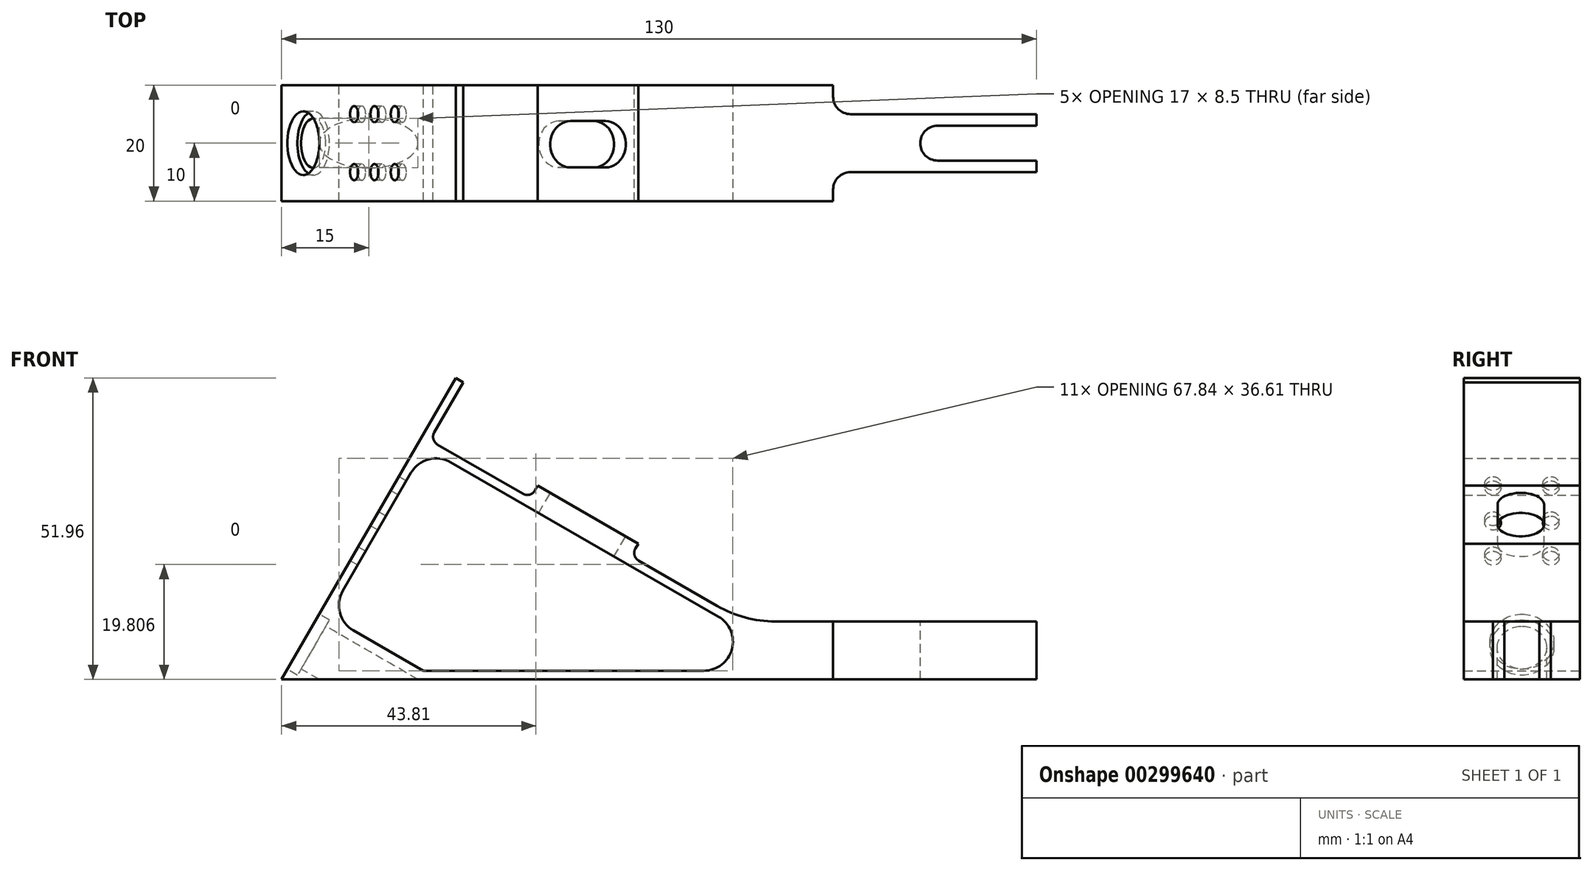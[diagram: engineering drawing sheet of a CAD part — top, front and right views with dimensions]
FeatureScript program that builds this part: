
annotation { "Feature Type Name" : "Feature", "Feature Type Description" : "" }
export const myFeature = defineFeature(function(context is Context, id is Id, definition is map)
    precondition{}
    {
        {
            var Q0;
            Q0=qCreatedBy(makeId("Front.planeOp"),FACE);
            var sketch = newSketch(context, id + "F0", { "sketchPlane" : qUnion([Q0])});
            skLineSegment(sketch, "E0", {"start": v(-65, 0) * mm, "end": v(-35, 51.96) * mm});
            skLineSegment(sketch, "E1", {"start": v(-35, 51.96) * mm, "end": v(-33.7, 51.21) * mm});
            skLineSegment(sketch, "E2", {"start": v(-33.7, 51.21) * mm, "end": v(-38.7, 42.55) * mm});
            skLineSegment(sketch, "E3", {"start": v(-38.15, 40.5) * mm, "end": v(-23.43, 32) * mm});
            skLineSegment(sketch, "E4", {"start": v(-21.38, 32.55) * mm, "end": v(-20.88, 33.42) * mm});
            skLineSegment(sketch, "E5", {"start": v(-20.88, 33.42) * mm, "end": v(-3.56, 23.42) * mm});
            skLineSegment(sketch, "E6", {"start": v(-3.56, 23.42) * mm, "end": v(-4.06, 22.55) * mm});
            skLineSegment(sketch, "E7", {"start": v(-3.51, 20.5) * mm, "end": v(10.04, 12.68) * mm});
            skLineSegment(sketch, "E8", {"start": v(20.04, 10) * mm, "end": v(65, 10) * mm});
            skLineSegment(sketch, "E9", {"start": v(65, 10) * mm, "end": v(65, 0) * mm});
            skLineSegment(sketch, "E10", {"start": v(-65, 0) * mm, "end": v(65, 0) * mm});
            skLineSegment(sketch, "E11", {"start": v(-22.13, 31.25) * mm, "end": v(-55.19, 50.34) * mm, "construction": true});
            skPoint(sketch, "E12.visualSharp", {"position": v(14.68, 10) * mm});
            skArc(sketch, "E12.filletArc", {"start": v(10.04, 12.68) * mm, "mid": v(14.86, 10.68) * mm, "end": v(20.04, 10) * mm});
            skPoint(sketch, "E13.visualSharp", {"position": v(-4.8, 21.25) * mm});
            skArc(sketch, "E13.filletArc", {"start": v(-4.06, 22.55) * mm, "mid": v(-4.2, 21.41) * mm, "end": v(-3.51, 20.5) * mm});
            skPoint(sketch, "E14.visualSharp", {"position": v(-22.13, 31.25) * mm});
            skArc(sketch, "E14.filletArc", {"start": v(-23.43, 32) * mm, "mid": v(-22.3, 31.85) * mm, "end": v(-21.38, 32.55) * mm});
            skPoint(sketch, "E15.visualSharp", {"position": v(-39.45, 41.25) * mm});
            skArc(sketch, "E15.filletArc", {"start": v(-38.7, 42.55) * mm, "mid": v(-38.85, 41.41) * mm, "end": v(-38.15, 40.5) * mm});
            skLineSegment(sketch, "E16", {"start": v(-54.45, 15.27) * mm, "end": v(-42.7, 35.62) * mm});
            skLineSegment(sketch, "E17", {"start": v(-35.87, 37.45) * mm, "end": v(10.24, 10.83) * mm});
            skLineSegment(sketch, "E18", {"start": v(7.74, 1.5) * mm, "end": v(-40.6, 1.5) * mm});
            skLineSegment(sketch, "E19", {"start": v(-40.6, 1.5) * mm, "end": v(-52.62, 8.44) * mm});
            skPoint(sketch, "E20.visualSharp", {"position": v(26.4, 1.5) * mm});
            skArc(sketch, "E20.filletArc", {"start": v(7.74, 1.5) * mm, "mid": v(12.57, 5.2) * mm, "end": v(10.24, 10.83) * mm});
            skPoint(sketch, "E21.visualSharp", {"position": v(-56.95, 10.94) * mm});
            skArc(sketch, "E21.filletArc", {"start": v(-54.45, 15.27) * mm, "mid": v(-54.95, 11.48) * mm, "end": v(-52.62, 8.44) * mm});
            skPoint(sketch, "E22.visualSharp", {"position": v(-40.2, 39.95) * mm});
            skArc(sketch, "E22.filletArc", {"start": v(-35.87, 37.45) * mm, "mid": v(-39.66, 37.95) * mm, "end": v(-42.7, 35.62) * mm});
            skSolve(sketch);
        }
        {
            var Q0;
            Q0=makeQuery(id+"F0.imprint","IMPRINT",FACE,{"disambiguationData":[TD([[makeQuery(id+"F0.imprint","IMPRINT",EDGE,{"derivedFrom":sQuery(id+"F0.wireOp",EDGE,"E0")}),-1.0]])]});
            extrude(context, id + "F1", {"entities" : qUnion([Q0]), "depth" : 20 * mm});
        }
        {
            var Q0;
            Q0=makeQuery(id+"F1.opExtrude","SWEPT_FACE",FACE,{"disambiguationData":[OSD([sQuery(id+"F0.wireOp",EDGE,"E8")])]});
            var sketch = newSketch(context, id + "F2", { "sketchPlane" : qUnion([Q0])});
            skArc(sketch, "E23", {"start": v(48, -7) * mm, "mid": v(45, -10) * mm, "end": v(48, -13) * mm});
            skLineSegment(sketch, "E24", {"start": v(48, -7) * mm, "end": v(65, -7) * mm});
            skLineSegment(sketch, "E25", {"start": v(48, -13) * mm, "end": v(65, -13) * mm});
            skLineSegment(sketch, "E26", {"start": v(65, -13) * mm, "end": v(65, -7) * mm});
            skLineSegment(sketch, "E27", {"start": v(65, -2.04) * mm, "end": v(65, -17.96) * mm});
            skLineSegment(sketch, "E28", {"start": v(65, -5) * mm, "end": v(33, -5) * mm});
            skLineSegment(sketch, "E29", {"start": v(30, -2) * mm, "end": v(30, 0) * mm});
            skLineSegment(sketch, "E30", {"start": v(30, -18) * mm, "end": v(30, -20) * mm});
            skLineSegment(sketch, "E31", {"start": v(33, -15) * mm, "end": v(65, -15) * mm});
            skPoint(sketch, "E32.visualSharp", {"position": v(30, -15) * mm});
            skArc(sketch, "E32.filletArc", {"start": v(33, -15) * mm, "mid": v(30.88, -15.88) * mm, "end": v(30, -18) * mm});
            skPoint(sketch, "E33.visualSharp", {"position": v(30, -5) * mm});
            skArc(sketch, "E33.filletArc", {"start": v(30, -2) * mm, "mid": v(30.88, -4.12) * mm, "end": v(33, -5) * mm});
            skLineSegment(sketch, "E34", {"start": v(30, 0) * mm, "end": v(65, 0) * mm});
            skLineSegment(sketch, "E35", {"start": v(65, 0) * mm, "end": v(65, -5) * mm});
            skLineSegment(sketch, "E36", {"start": v(65, -15) * mm, "end": v(65, -20) * mm});
            skLineSegment(sketch, "E37", {"start": v(65, -20) * mm, "end": v(30, -20) * mm});
            skSolve(sketch);
        }
        {
            var Q0;
            Q0=makeQuery(id+"F2.imprint","IMPRINT",FACE,{"disambiguationData":[TD([[makeQuery(id+"F2.imprint","IMPRINT",EDGE,{"derivedFrom":sQuery(id+"F2.wireOp",EDGE,"E30")}),1.0]])]});
            var Q1;
            Q1=makeQuery(id+"F2.imprint","IMPRINT",FACE,{"disambiguationData":[TD([[makeQuery(id+"F2.imprint","IMPRINT",EDGE,{"derivedFrom":sQuery(id+"F2.wireOp",EDGE,"E23")}),1.0]])]});
            var Q2;
            {var subQ1=sQuery(id+"F2.wireOp",EDGE,"E28");Q2=makeQuery(id+"F2.imprint","IMPRINT",FACE,{"disambiguationData":[TD([[makeQuery(id+"F2.imprint","IMPRINT",EDGE,{"derivedFrom":subQ1}),-1.0]])]});}
            extrude(context, id + "F3", {"entities" : qUnion([Q0, Q1, Q2]), "operationType" : NewBodyOperationType.REMOVE, "oppositeDirection" : true, "depth" : 25 * mm});
        }
        {
            var Q0;
            Q0=makeQuery(id+"F1.opExtrude","SWEPT_FACE",FACE,{"disambiguationData":[OSD([sQuery(id+"F0.wireOp",EDGE,"E5")])]});
            cPlane(context, id + "F4", {"entities" : qUnion([Q0]), "cplaneType" : CPlaneType.OFFSET, "offset" : 0 * mm, "width" : 150 * mm, "height" : 150 * mm});
        }
        {
            var Q0;
            Q0=qCreatedBy(id+"F4.planeOp",FACE);
            var sketch = newSketch(context, id + "F5", { "sketchPlane" : qUnion([Q0])});
            skArc(sketch, "E38", {"start": v(-28.3, -6.2) * mm, "mid": v(-32.3, -10.2) * mm, "end": v(-28.3, -14.2) * mm});
            skArc(sketch, "E39", {"start": v(-21.3, -14.2) * mm, "mid": v(-17.3, -10.2) * mm, "end": v(-21.3, -6.2) * mm});
            skLineSegment(sketch, "E40", {"start": v(-28.3, -6.2) * mm, "end": v(-21.3, -6.2) * mm});
            skLineSegment(sketch, "E41", {"start": v(-28.3, -14.2) * mm, "end": v(-21.3, -14.2) * mm});
            skSolve(sketch);
        }
        {
            var Q0;
            Q0 = qSketchRegion(id + "F5", true);
            extrude(context, id + "F6", {"entities" : qUnion([Q0]), "operationType" : NewBodyOperationType.REMOVE, "endBound" : BoundingType.UP_TO_NEXT, "oppositeDirection" : true, "depth" : 25 * mm});
        }
        {
            var Q0;
            Q0=makeQuery(id+"F1.opExtrude","SWEPT_FACE",FACE,{"disambiguationData":[OSD([sQuery(id+"F0.wireOp",EDGE,"E0")])]});
            cPlane(context, id + "F7", {"entities" : qUnion([Q0]), "cplaneType" : CPlaneType.OFFSET, "offset" : 0 * mm, "width" : 150 * mm, "height" : 150 * mm});
        }
        {
            var Q0;
            Q0=qCreatedBy(id+"F7.planeOp",FACE);
            var sketch = newSketch(context, id + "F8", { "sketchPlane" : qUnion([Q0])});
            skCircle(sketch, "E42", {"center": v(5, -7.5) * mm, "radius": 1.4 * mm});
            skCircle(sketch, "E43.0.1.0", {"center": v(5, -0.5) * mm, "radius": 1.4 * mm});
            skCircle(sketch, "E43.0.2.0", {"center": v(5, 6.5) * mm, "radius": 1.4 * mm});
            skCircle(sketch, "E43.1.0.0", {"center": v(15, -7.5) * mm, "radius": 1.4 * mm});
            skCircle(sketch, "E43.1.1.0", {"center": v(15, -0.5) * mm, "radius": 1.4 * mm});
            skCircle(sketch, "E43.1.2.0", {"center": v(15, 6.5) * mm, "radius": 1.4 * mm});
            skLineSegment(sketch, "E43.direction1", {"start": v(5, -7.5) * mm, "end": v(15, -7.5) * mm, "construction": true});
            skLineSegment(sketch, "E43.direction2", {"start": v(5, -7.5) * mm, "end": v(5, -0.5) * mm, "construction": true});
            skLineSegment(sketch, "E44", {"start": v(10, 29.37) * mm, "end": v(10, -36.54) * mm, "construction": true});
            skCircle(sketch, "E45", {"center": v(10, -25) * mm, "radius": 5.5 * mm});
            skCircle(sketch, "E46", {"center": v(10, -25) * mm, "radius": 4.25 * mm});
            skSolve(sketch);
        }
        {
            var Q0;
            Q0=makeQuery(id+"F8.imprint","IMPRINT",FACE,{"disambiguationData":[TD([[makeQuery(id+"F8.imprint","IMPRINT",EDGE,{"derivedFrom":sQuery(id+"F8.wireOp",EDGE,"E42")}),1.0]])]});
            var Q1;
            Q1=makeQuery(id+"F8.imprint","IMPRINT",FACE,{"disambiguationData":[TD([[makeQuery(id+"F8.imprint","IMPRINT",EDGE,{"derivedFrom":sQuery(id+"F8.wireOp",EDGE,"E43.0.1.0")}),1.0]])]});
            var Q2;
            Q2=makeQuery(id+"F8.imprint","IMPRINT",FACE,{"disambiguationData":[TD([[makeQuery(id+"F8.imprint","IMPRINT",EDGE,{"derivedFrom":sQuery(id+"F8.wireOp",EDGE,"E43.0.2.0")}),1.0]])]});
            var Q3;
            Q3=makeQuery(id+"F8.imprint","IMPRINT",FACE,{"disambiguationData":[TD([[makeQuery(id+"F8.imprint","IMPRINT",EDGE,{"derivedFrom":sQuery(id+"F8.wireOp",EDGE,"E43.1.0.0")}),1.0]])]});
            var Q4;
            Q4=makeQuery(id+"F8.imprint","IMPRINT",FACE,{"disambiguationData":[TD([[makeQuery(id+"F8.imprint","IMPRINT",EDGE,{"derivedFrom":sQuery(id+"F8.wireOp",EDGE,"E43.1.1.0")}),1.0]])]});
            var Q5;
            Q5=makeQuery(id+"F8.imprint","IMPRINT",FACE,{"disambiguationData":[TD([[makeQuery(id+"F8.imprint","IMPRINT",EDGE,{"derivedFrom":sQuery(id+"F8.wireOp",EDGE,"E43.1.2.0")}),1.0]])]});
            extrude(context, id + "F9", {"entities" : qUnion([Q0, Q1, Q2, Q3, Q4, Q5]), "operationType" : NewBodyOperationType.REMOVE, "endBound" : BoundingType.UP_TO_NEXT, "oppositeDirection" : true, "depth" : 25 * mm});
        }
        {
            var Q0;
            Q0=makeQuery(id+"F8.imprint","IMPRINT",FACE,{"disambiguationData":[TD([[makeQuery(id+"F8.imprint","IMPRINT",EDGE,{"derivedFrom":sQuery(id+"F8.wireOp",EDGE,"E46")}),1.0]])]});
            extrude(context, id + "F10", {"entities" : qUnion([Q0]), "operationType" : NewBodyOperationType.REMOVE, "endBound" : BoundingType.THROUGH_ALL, "oppositeDirection" : true, "depth" : 25 * mm});
        }
        {
            var Q0;
            Q0=makeQuery(id+"F8.imprint","IMPRINT",FACE,{"disambiguationData":[TD([[makeQuery(id+"F8.imprint","IMPRINT",EDGE,{"derivedFrom":sQuery(id+"F8.wireOp",EDGE,"E45")}),1.0]])]});
            extrude(context, id + "F11", {"entities" : qUnion([Q0]), "operationType" : NewBodyOperationType.REMOVE, "oppositeDirection" : true, "depth" : 2 * mm});
        }
    });
